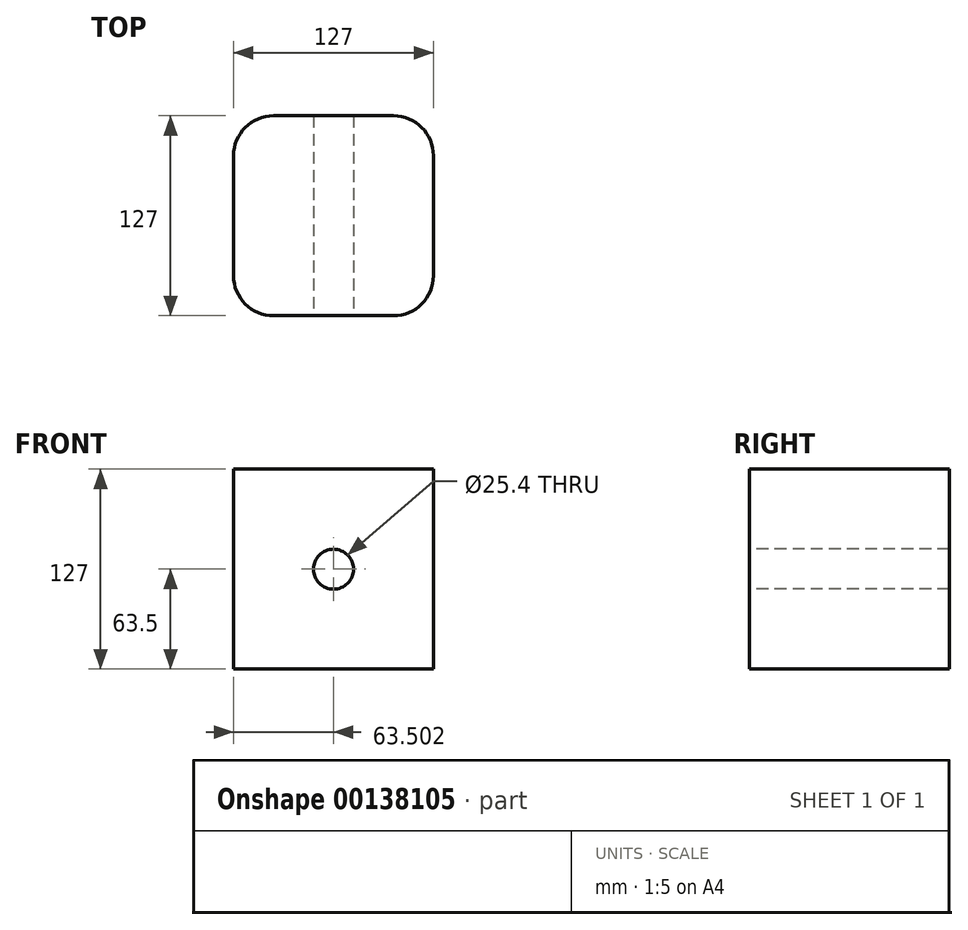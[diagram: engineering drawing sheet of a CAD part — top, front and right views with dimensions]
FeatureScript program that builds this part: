
annotation { "Feature Type Name" : "Feature", "Feature Type Description" : "" }
export const myFeature = defineFeature(function(context is Context, id is Id, definition is map)
    precondition{}
    {
        {
            var Q0;
            Q0=qCreatedBy(makeId("Top.planeOp"),FACE);
            var sketch = newSketch(context, id + "F0", { "sketchPlane" : qUnion([Q0])});
            skLineSegment(sketch, "E0", {"start": v(-31.28, 68.55) * mm, "end": v(70.32, 68.55) * mm});
            skLineSegment(sketch, "E1", {"start": v(70.32, 68.55) * mm, "end": v(70.32, -58.45) * mm});
            skLineSegment(sketch, "E2", {"start": v(70.32, -58.45) * mm, "end": v(-56.68, -58.45) * mm});
            skLineSegment(sketch, "E3", {"start": v(-56.68, 43.15) * mm, "end": v(-56.68, -58.45) * mm});
            skPoint(sketch, "E4.visualSharp", {"position": v(-56.68, 68.55) * mm});
            skArc(sketch, "E4.filletArc", {"start": v(-31.28, 68.55) * mm, "mid": v(-49.24, 61.11) * mm, "end": v(-56.68, 43.15) * mm});
            skSolve(sketch);
        }
        {
            var Q0;
            Q0 = qSketchRegion(id + "F0", true);
            extrude(context, id + "F1", {"entities" : qUnion([Q0]), "depth" : 127 * mm});
        }
        {
            var Q0;
            Q0=makeQuery(id+"F1.opExtrude","SWEPT_EDGE",EDGE,{"disambiguationData":[OSD([sQuery(id+"F0.wireOp",EDGE,"E0"),sQuery(id+"F0.wireOp",EDGE,"E1")])]});
            var Q1;
            Q1=makeQuery(id+"F1.opExtrude","SWEPT_EDGE",EDGE,{"disambiguationData":[OSD([sQuery(id+"F0.wireOp",EDGE,"E1"),sQuery(id+"F0.wireOp",EDGE,"E2")])]});
            var Q2;
            Q2=makeQuery(id+"F1.opExtrude","SWEPT_EDGE",EDGE,{"disambiguationData":[OSD([sQuery(id+"F0.wireOp",EDGE,"E2"),sQuery(id+"F0.wireOp",EDGE,"E3")])]});
            fillet(context, id + "F2", {"entities" : qUnion([Q0, Q1, Q2]), "radius" : 25.4 * mm, "tangentPropagation" : true, "allowEdgeOverflow" : false});
        }
        {
            var Q0;
            Q0=makeQuery(id+"F1.opExtrude","SWEPT_FACE",FACE,{"disambiguationData":[OSD([sQuery(id+"F0.wireOp",EDGE,"E2")])]});
            var sketch = newSketch(context, id + "F3", { "sketchPlane" : qUnion([Q0])});
            skCircle(sketch, "E5", {"center": v(6.82, 63.5) * mm, "radius": 12.7 * mm});
            skSolve(sketch);
        }
        {
            var Q0;
            Q0 = qSketchRegion(id + "F3", true);
            extrude(context, id + "F4", {"entities" : qUnion([Q0]), "operationType" : NewBodyOperationType.REMOVE, "endBound" : BoundingType.THROUGH_ALL, "oppositeDirection" : true, "depth" : 25.4 * mm});
        }
    });
